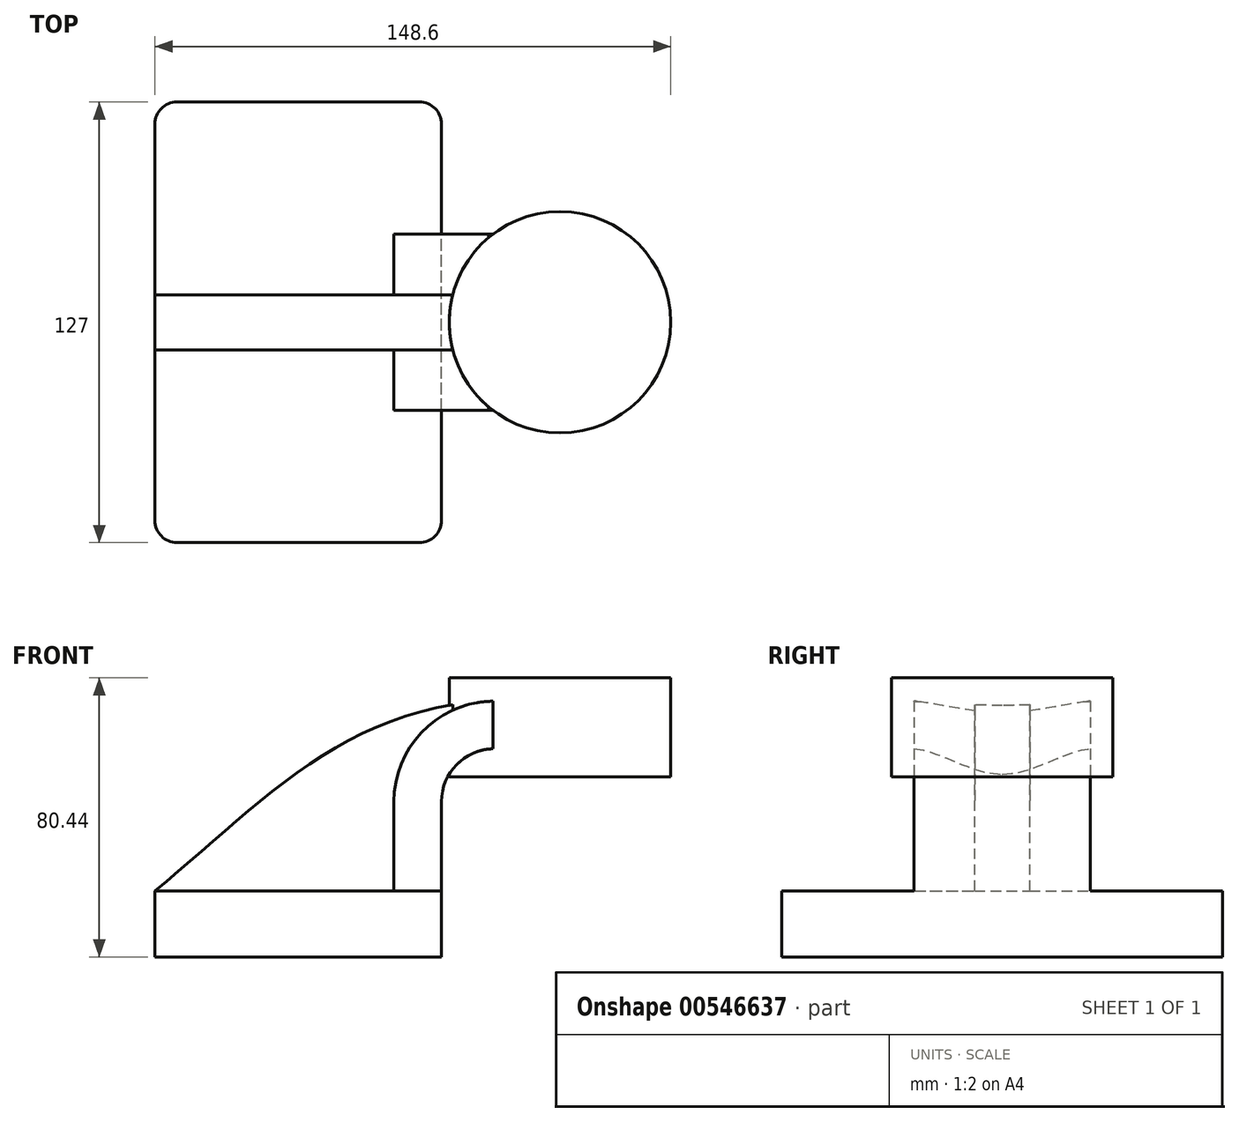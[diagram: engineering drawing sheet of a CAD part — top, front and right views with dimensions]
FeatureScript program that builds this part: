
annotation { "Feature Type Name" : "Feature", "Feature Type Description" : "" }
export const myFeature = defineFeature(function(context is Context, id is Id, definition is map)
    precondition{}
    {
        {
            var Q0;
            Q0=qCreatedBy(makeId("Front.planeOp"),FACE);
            var sketch = newSketch(context, id + "F0", { "sketchPlane" : qUnion([Q0])});
            skLineSegment(sketch, "E0.bottom", {"start": v(-41.28, -9.53) * mm, "end": v(41.28, -9.53) * mm});
            skLineSegment(sketch, "E0.top", {"start": v(-41.28, 9.53) * mm, "end": v(41.28, 9.53) * mm});
            skLineSegment(sketch, "E0.left", {"start": v(-41.28, -9.53) * mm, "end": v(-41.28, 9.53) * mm});
            skLineSegment(sketch, "E0.right", {"start": v(41.28, -9.53) * mm, "end": v(41.28, 9.53) * mm});
            skPoint(sketch, "E0.middle", {"position": v(0, 0) * mm});
            skLineSegment(sketch, "E1.bottom", {"start": v(107.32, 42.33) * mm, "end": v(56.52, 42.33) * mm});
            skLineSegment(sketch, "E1.top", {"start": v(107.32, 70.9) * mm, "end": v(56.52, 70.9) * mm});
            skLineSegment(sketch, "E1.left", {"start": v(107.31, 42.33) * mm, "end": v(107.31, 70.9) * mm});
            skLineSegment(sketch, "E1.right", {"start": v(56.51, 42.33) * mm, "end": v(56.51, 70.9) * mm});
            skPoint(sketch, "E1.middle", {"position": v(81.92, 56.62) * mm});
            skLineSegment(sketch, "E2", {"start": v(41.28, 9.53) * mm, "end": v(41.28, 35.22) * mm});
            skArc(sketch, "E3", {"start": v(41.28, 35.22) * mm, "mid": v(45.74, 46) * mm, "end": v(56.52, 50.46) * mm});
            skLineSegment(sketch, "E4", {"start": v(56.52, 50.46) * mm, "end": v(85.7, 50.46) * mm});
            skArc(sketch, "E5.0", {"start": v(27.56, 35.22) * mm, "mid": v(36.04, 55.7) * mm, "end": v(56.52, 64.18) * mm});
            skLineSegment(sketch, "E5.1", {"start": v(27.56, 9.53) * mm, "end": v(27.56, 35.22) * mm});
            skFitSpline(sketch, "E6", {"points": [v(-41.28, 9.53) * mm, v(56.52, 64.18) * mm], "startDerivative": vector(86.38, 70.4) * mm, "endDerivative": vector(129.42, 2.6) * mm});
            skLineSegment(sketch, "E7", {"start": v(71.1, 42.33) * mm, "end": v(71.1, 70.9) * mm});
            skPoint(sketch, "E7.startSnap0", {"position": v(81.92, 42.33) * mm});
            skPoint(sketch, "E7.startSnap1", {"position": v(71.1, 63.92) * mm});
            skLineSegment(sketch, "E8", {"start": v(56.52, 42.33) * mm, "end": v(56.52, 70.9) * mm});
            skLineSegment(sketch, "E9", {"start": v(75.4, 42.33) * mm, "end": v(75.4, 70.9) * mm});
            skLineSegment(sketch, "E10.0", {"start": v(56.52, 64.18) * mm, "end": v(85.7, 64.18) * mm});
            skSolve(sketch);
        }
        {
            var Q0;
            Q0=makeQuery(id+"F0.imprint","IMPRINT",FACE,{"disambiguationData":[TD([[makeQuery(id+"F0.imprint","IMPRINT",EDGE,{"derivedFrom":sQuery(id+"F0.wireOp",EDGE,"E0.bottom")}),1.0]])]});
            extrude(context, id + "F1", {"entities" : qUnion([Q0]), "endBound" : BoundingType.SYMMETRIC, "depth" : 127 * mm, "offsetDistance" : 25.4 * mm});
        }
        {
            var Q0;
            {var subQ3=sQuery(id+"F0.wireOp",EDGE,"E5.1");Q0=makeQuery(id+"F0.imprint","IMPRINT",FACE,{"disambiguationData":[TD([[makeQuery(id+"F0.imprint","IMPRINT",EDGE,{"derivedFrom":subQ3}),1.0]])]});}
            extrude(context, id + "F2", {"entities" : qUnion([Q0]), "operationType" : NewBodyOperationType.ADD, "endBound" : BoundingType.SYMMETRIC, "depth" : 15.88 * mm, "offsetDistance" : 25.4 * mm});
        }
        {
            var Q0;
            {var subQ0=sQuery(id+"F0.wireOp",EDGE,"E2");Q0=makeQuery(id+"F0.imprint","IMPRINT",FACE,{"disambiguationData":[TD([[makeQuery(id+"F0.imprint","IMPRINT",EDGE,{"derivedFrom":subQ0}),1.0]])]});}
            extrude(context, id + "F3", {"entities" : qUnion([Q0]), "operationType" : NewBodyOperationType.ADD, "endBound" : BoundingType.SYMMETRIC, "depth" : 50.8 * mm, "offsetDistance" : 25.4 * mm});
        }
        {
            var Q0;
            Q0=makeQuery(id+"F1.opExtrude","CAP_EDGE",EDGE,{"disambiguationData":[OSD([sQuery(id+"F0.wireOp",EDGE,"E0.left")])],"isStart":false});
            var Q1;
            Q1=makeQuery(id+"F1.opExtrude","CAP_EDGE",EDGE,{"disambiguationData":[OSD([sQuery(id+"F0.wireOp",EDGE,"E0.right")])],"isStart":false});
            var Q2;
            Q2=makeQuery(id+"F1.opExtrude","CAP_EDGE",EDGE,{"disambiguationData":[OSD([sQuery(id+"F0.wireOp",EDGE,"E0.right")])],"isStart":true});
            var Q3;
            Q3=makeQuery(id+"F1.opExtrude","CAP_EDGE",EDGE,{"disambiguationData":[OSD([sQuery(id+"F0.wireOp",EDGE,"E0.left")])],"isStart":true});
            fillet(context, id + "F4", {"entities" : qUnion([Q0, Q1, Q2, Q3]), "radius" : 6.35 * mm, "tangentPropagation" : true, "allowEdgeOverflow" : false});
        }
        {
            var Q0;
            {var subQ4=sQuery(id+"F0.wireOp",EDGE,"E1.left");Q0=makeQuery(id+"F0.imprint","IMPRINT",FACE,{"disambiguationData":[TD([[makeQuery(id+"F0.imprint","IMPRINT",EDGE,{"derivedFrom":subQ4}),1.0]])]});}
            var Q1;
            Q1=sQuery(id+"F0.wireOp",EDGE,"E9");
            revolve(context, id + "F5", {"operationType" : NewBodyOperationType.ADD, "entities" : qUnion([Q0]), "axis" : qUnion([Q1]), "revolveType" : RevolveType.FULL});
        }
    });
